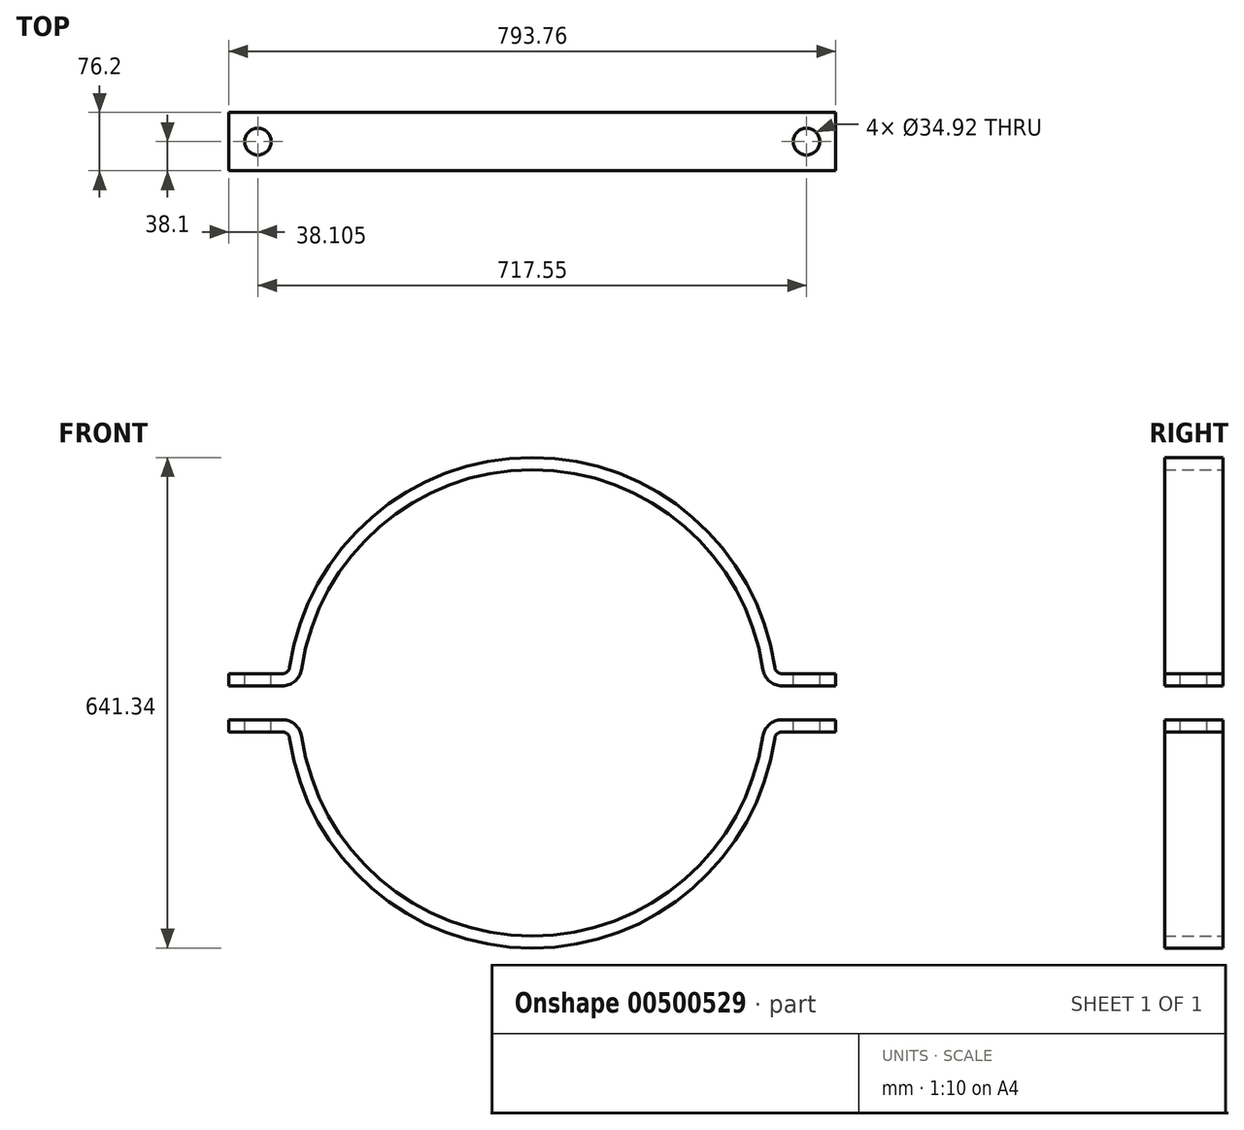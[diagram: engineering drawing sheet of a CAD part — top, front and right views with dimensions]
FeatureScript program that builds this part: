
annotation { "Feature Type Name" : "Feature", "Feature Type Description" : "" }
export const myFeature = defineFeature(function(context is Context, id is Id, definition is map)
    precondition{}
    {
        {
            var Q0;
            Q0=qCreatedBy(makeId("Front.planeOp"),FACE);
            var sketch = newSketch(context, id + "F0", { "sketchPlane" : qUnion([Q0])});
            skArc(sketch, "E0", {"start": v(303.99, 22.22) * mm, "mid": v(0, 304.8) * mm, "end": v(-303.99, 22.22) * mm});
            skArc(sketch, "E1", {"start": v(318.4, 38.1) * mm, "mid": v(0, 320.68) * mm, "end": v(-318.4, 38.1) * mm});
            skLineSegment(sketch, "E2.bottom", {"start": v(396.88, 38.1) * mm, "end": v(318.4, 38.1) * mm});
            skLineSegment(sketch, "E2.top", {"start": v(396.88, 22.23) * mm, "end": v(303.99, 22.23) * mm});
            skLineSegment(sketch, "E2.left", {"start": v(396.88, 38.1) * mm, "end": v(396.88, 22.23) * mm});
            skLineSegment(sketch, "E2.right", {"start": v(-396.88, 38.1) * mm, "end": v(-396.88, 22.22) * mm});
            skPoint(sketch, "E2.middle", {"position": v(0, 30.16) * mm});
            skLineSegment(sketch, "E3.trimOffspring", {"start": v(-318.4, 38.1) * mm, "end": v(-396.88, 38.1) * mm});
            skLineSegment(sketch, "E4.trimOffspring", {"start": v(-303.99, 22.22) * mm, "end": v(-396.88, 22.22) * mm});
            skLineSegment(sketch, "E5.MirrorCS", {"start": v(-396.88, -38.1) * mm, "end": v(-396.88, -22.22) * mm});
            skLineSegment(sketch, "E6.MirrorCS", {"start": v(396.88, -38.1) * mm, "end": v(396.88, -22.23) * mm});
            skArc(sketch, "E7.MirrorCS", {"start": v(318.4, -38.1) * mm, "mid": v(0, -320.68) * mm, "end": v(-318.4, -38.1) * mm});
            skLineSegment(sketch, "E8.MirrorCS", {"start": v(-303.99, -22.22) * mm, "end": v(-396.88, -22.22) * mm});
            skLineSegment(sketch, "E9.MirrorCS", {"start": v(-318.4, -38.1) * mm, "end": v(-396.88, -38.1) * mm});
            skPoint(sketch, "E10.MirrorP", {"position": v(0, -30.16) * mm});
            skArc(sketch, "E11.MirrorCS", {"start": v(303.99, -22.22) * mm, "mid": v(0, -304.8) * mm, "end": v(-303.99, -22.22) * mm});
            skLineSegment(sketch, "E12.MirrorCS", {"start": v(396.88, -38.1) * mm, "end": v(318.4, -38.1) * mm});
            skLineSegment(sketch, "E13.MirrorCS", {"start": v(396.88, -22.23) * mm, "end": v(303.99, -22.23) * mm});
            skSolve(sketch);
        }
        {
            var Q0;
            Q0 = qSketchRegion(id + "F0", true);
            extrude(context, id + "F1", {"entities" : qUnion([Q0]), "endBound" : BoundingType.SYMMETRIC, "depth" : 76.2 * mm});
        }
        {
            var Q0;
            Q0=makeQuery(id+"F1.opExtrude","SWEPT_EDGE",EDGE,{"disambiguationData":[OSD([sQuery(id+"F0.wireOp",EDGE,"E1"),sQuery(id+"F0.wireOp",EDGE,"E3.trimOffspring")])]});
            var Q1;
            Q1=makeQuery(id+"F1.opExtrude","SWEPT_EDGE",EDGE,{"disambiguationData":[OSD([sQuery(id+"F0.wireOp",EDGE,"E7.MirrorCS"),sQuery(id+"F0.wireOp",EDGE,"E9.MirrorCS")])]});
            var Q2;
            Q2=makeQuery(id+"F1.opExtrude","SWEPT_EDGE",EDGE,{"disambiguationData":[OSD([sQuery(id+"F0.wireOp",EDGE,"E1"),sQuery(id+"F0.wireOp",EDGE,"E2.bottom")])]});
            var Q3;
            Q3=makeQuery(id+"F1.opExtrude","SWEPT_EDGE",EDGE,{"disambiguationData":[OSD([sQuery(id+"F0.wireOp",EDGE,"E7.MirrorCS"),sQuery(id+"F0.wireOp",EDGE,"E12.MirrorCS")])]});
            fillet(context, id + "F2", {"entities" : qUnion([Q0, Q1, Q2, Q3]), "radius" : 9.52 * mm, "tangentPropagation" : true, "allowEdgeOverflow" : false});
        }
        {
            var Q0;
            Q0=makeQuery(id+"F1.opExtrude","SWEPT_EDGE",EDGE,{"disambiguationData":[OSD([sQuery(id+"F0.wireOp",EDGE,"E0"),sQuery(id+"F0.wireOp",EDGE,"E4.trimOffspring")])]});
            var Q1;
            Q1=makeQuery(id+"F1.opExtrude","SWEPT_EDGE",EDGE,{"disambiguationData":[OSD([sQuery(id+"F0.wireOp",EDGE,"E8.MirrorCS"),sQuery(id+"F0.wireOp",EDGE,"E11.MirrorCS")])]});
            var Q2;
            Q2=makeQuery(id+"F1.opExtrude","SWEPT_EDGE",EDGE,{"disambiguationData":[OSD([sQuery(id+"F0.wireOp",EDGE,"E0"),sQuery(id+"F0.wireOp",EDGE,"E2.top")])]});
            var Q3;
            Q3=makeQuery(id+"F1.opExtrude","SWEPT_EDGE",EDGE,{"disambiguationData":[OSD([sQuery(id+"F0.wireOp",EDGE,"E11.MirrorCS"),sQuery(id+"F0.wireOp",EDGE,"E13.MirrorCS")])]});
            fillet(context, id + "F3", {"entities" : qUnion([Q0, Q1, Q2, Q3]), "radius" : 25.4 * mm, "tangentPropagation" : true, "allowEdgeOverflow" : false});
        }
        {
            var Q0;
            Q0=makeQuery(id+"F1.opExtrude","SWEPT_FACE",FACE,{"disambiguationData":[OSD([sQuery(id+"F0.wireOp",EDGE,"E3.trimOffspring")])]});
            var sketch = newSketch(context, id + "F4", { "sketchPlane" : qUnion([Q0])});
            skCircle(sketch, "E14", {"center": v(-358.78, 0) * mm, "radius": 17.46 * mm});
            skCircle(sketch, "E15.MirrorC", {"center": v(358.78, 0) * mm, "radius": 17.46 * mm});
            skSolve(sketch);
        }
        {
            var Q0;
            Q0 = qSketchRegion(id + "F4", true);
            extrude(context, id + "F5", {"entities" : qUnion([Q0]), "operationType" : NewBodyOperationType.REMOVE, "endBound" : BoundingType.SYMMETRIC, "oppositeDirection" : true, "depth" : 152.4 * mm});
        }
    });
